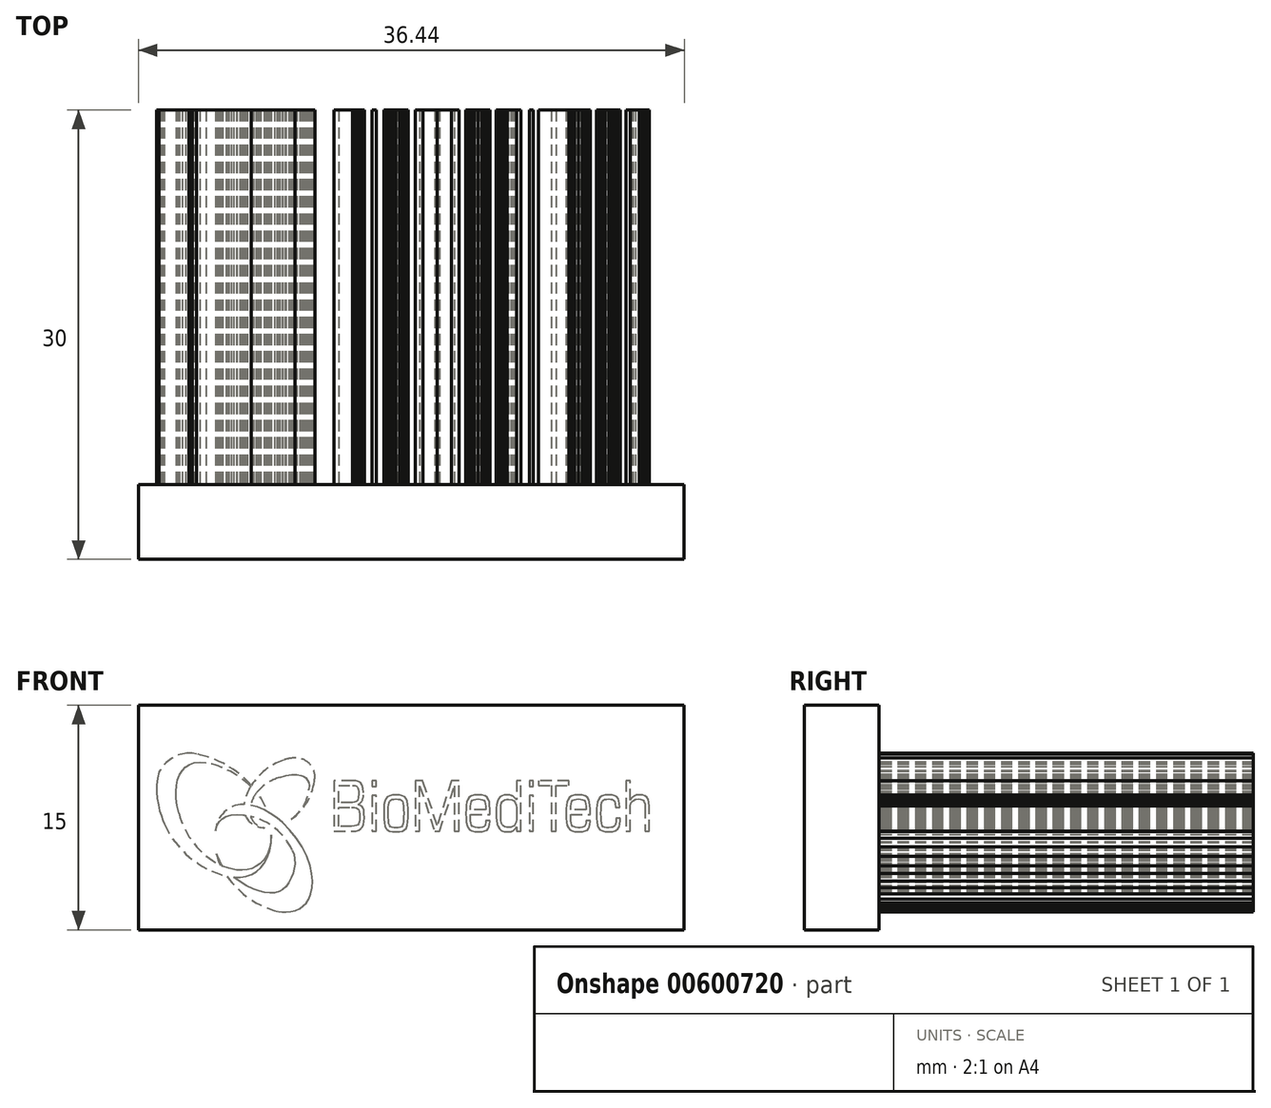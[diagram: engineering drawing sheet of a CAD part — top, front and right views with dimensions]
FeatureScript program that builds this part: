
annotation { "Feature Type Name" : "Feature", "Feature Type Description" : "" }
export const myFeature = defineFeature(function(context is Context, id is Id, definition is map)
    precondition{}
    {
        {
            var Q0;
            Q0=qCreatedBy(makeId("Front.planeOp"),FACE);
            var sketch = newSketch(context, id + "F0", { "sketchPlane" : qUnion([Q0])});
            skLineSegment(sketch, "E0", {"start": v(36.62, 94.25) * mm, "end": v(36.5, 94.75) * mm});
            skLineSegment(sketch, "E1", {"start": v(36.5, 94.75) * mm, "end": v(36.44, 95.22) * mm});
            skLineSegment(sketch, "E2", {"start": v(36.44, 95.22) * mm, "end": v(36.42, 95.67) * mm});
            skLineSegment(sketch, "E3", {"start": v(36.42, 95.67) * mm, "end": v(36.45, 96.09) * mm});
            skLineSegment(sketch, "E4", {"start": v(36.45, 96.09) * mm, "end": v(36.53, 96.47) * mm});
            skLineSegment(sketch, "E5", {"start": v(36.53, 96.47) * mm, "end": v(36.65, 96.8) * mm});
            skLineSegment(sketch, "E6", {"start": v(36.65, 96.8) * mm, "end": v(36.83, 97.1) * mm});
            skLineSegment(sketch, "E7", {"start": v(36.83, 97.1) * mm, "end": v(37.05, 97.32) * mm});
            skLineSegment(sketch, "E8", {"start": v(37.05, 97.32) * mm, "end": v(37.33, 97.5) * mm});
            skLineSegment(sketch, "E9", {"start": v(37.33, 97.5) * mm, "end": v(37.65, 97.6) * mm});
            skLineSegment(sketch, "E10", {"start": v(37.65, 97.6) * mm, "end": v(38.01, 97.64) * mm});
            skLineSegment(sketch, "E11", {"start": v(38.01, 97.64) * mm, "end": v(38.43, 97.6) * mm});
            skLineSegment(sketch, "E12", {"start": v(39.27, 91.03) * mm, "end": v(39.33, 90.89) * mm});
            skLineSegment(sketch, "E13", {"start": v(39.33, 90.89) * mm, "end": v(39.38, 90.77) * mm});
            skLineSegment(sketch, "E14", {"start": v(39.55, 90.7) * mm, "end": v(39.43, 90.89) * mm});
            skLineSegment(sketch, "E15", {"start": v(39.43, 90.89) * mm, "end": v(39.35, 91.03) * mm});
            skLineSegment(sketch, "E16", {"start": v(40.46, 90.45) * mm, "end": v(39.95, 90.56) * mm});
            skLineSegment(sketch, "E17", {"start": v(39.95, 90.56) * mm, "end": v(39.55, 90.7) * mm});
            skLineSegment(sketch, "E18", {"start": v(42.79, 92.79) * mm, "end": v(42.76, 92.31) * mm});
            skLineSegment(sketch, "E19", {"start": v(42.76, 92.31) * mm, "end": v(42.67, 91.88) * mm});
            skLineSegment(sketch, "E20", {"start": v(42.67, 91.88) * mm, "end": v(42.51, 91.48) * mm});
            skLineSegment(sketch, "E21", {"start": v(42.51, 91.48) * mm, "end": v(42.3, 91.14) * mm});
            skLineSegment(sketch, "E22", {"start": v(42.3, 91.14) * mm, "end": v(42.03, 90.86) * mm});
            skLineSegment(sketch, "E23", {"start": v(42.03, 90.86) * mm, "end": v(41.78, 90.68) * mm});
            skLineSegment(sketch, "E24", {"start": v(41.78, 90.68) * mm, "end": v(41.5, 90.55) * mm});
            skLineSegment(sketch, "E25", {"start": v(41.5, 90.55) * mm, "end": v(41.18, 90.46) * mm});
            skLineSegment(sketch, "E26", {"start": v(41.18, 90.46) * mm, "end": v(40.84, 90.43) * mm});
            skLineSegment(sketch, "E27", {"start": v(40.84, 90.43) * mm, "end": v(40.46, 90.45) * mm});
            skLineSegment(sketch, "E28", {"start": v(40.27, 89.97) * mm, "end": v(40.7, 89.97) * mm});
            skLineSegment(sketch, "E29", {"start": v(40.7, 89.97) * mm, "end": v(41.1, 90.04) * mm});
            skLineSegment(sketch, "E30", {"start": v(41.1, 90.04) * mm, "end": v(41.47, 90.17) * mm});
            skLineSegment(sketch, "E31", {"start": v(41.47, 90.17) * mm, "end": v(41.8, 90.36) * mm});
            skLineSegment(sketch, "E32", {"start": v(41.8, 90.36) * mm, "end": v(42.07, 90.6) * mm});
            skLineSegment(sketch, "E33", {"start": v(42.07, 90.6) * mm, "end": v(42.3, 90.9) * mm});
            skLineSegment(sketch, "E34", {"start": v(42.3, 90.9) * mm, "end": v(42.53, 91.3) * mm});
            skLineSegment(sketch, "E35", {"start": v(42.53, 91.3) * mm, "end": v(42.68, 91.75) * mm});
            skLineSegment(sketch, "E36", {"start": v(42.68, 91.75) * mm, "end": v(42.77, 92.25) * mm});
            skLineSegment(sketch, "E37", {"start": v(42.77, 92.25) * mm, "end": v(42.79, 92.79) * mm});
            skLineSegment(sketch, "E38", {"start": v(43.31, 89) * mm, "end": v(43.01, 88.93) * mm});
            skLineSegment(sketch, "E39", {"start": v(43.01, 88.93) * mm, "end": v(42.68, 88.92) * mm});
            skLineSegment(sketch, "E40", {"start": v(42.68, 88.92) * mm, "end": v(42.34, 88.96) * mm});
            skLineSegment(sketch, "E41", {"start": v(42.34, 88.96) * mm, "end": v(41.98, 89.05) * mm});
            skLineSegment(sketch, "E42", {"start": v(41.98, 89.05) * mm, "end": v(41.61, 89.17) * mm});
            skLineSegment(sketch, "E43", {"start": v(41.61, 89.17) * mm, "end": v(41.14, 89.4) * mm});
            skLineSegment(sketch, "E44", {"start": v(41.14, 89.4) * mm, "end": v(40.69, 89.67) * mm});
            skLineSegment(sketch, "E45", {"start": v(40.69, 89.67) * mm, "end": v(40.27, 89.97) * mm});
            skLineSegment(sketch, "E46", {"start": v(44.18, 91.79) * mm, "end": v(44.3, 91.5) * mm});
            skLineSegment(sketch, "E47", {"start": v(44.3, 91.5) * mm, "end": v(44.35, 91.19) * mm});
            skLineSegment(sketch, "E48", {"start": v(44.35, 91.19) * mm, "end": v(44.36, 90.87) * mm});
            skLineSegment(sketch, "E49", {"start": v(44.36, 90.87) * mm, "end": v(44.32, 90.55) * mm});
            skLineSegment(sketch, "E50", {"start": v(44.32, 90.55) * mm, "end": v(44.24, 90.23) * mm});
            skLineSegment(sketch, "E51", {"start": v(44.24, 90.23) * mm, "end": v(44.13, 89.93) * mm});
            skLineSegment(sketch, "E52", {"start": v(44.13, 89.93) * mm, "end": v(43.96, 89.61) * mm});
            skLineSegment(sketch, "E53", {"start": v(43.96, 89.61) * mm, "end": v(43.77, 89.34) * mm});
            skLineSegment(sketch, "E54", {"start": v(43.77, 89.34) * mm, "end": v(43.55, 89.13) * mm});
            skLineSegment(sketch, "E55", {"start": v(43.55, 89.13) * mm, "end": v(43.31, 89) * mm});
            skLineSegment(sketch, "E56", {"start": v(40.9, 94.12) * mm, "end": v(40.98, 94.11) * mm});
            skLineSegment(sketch, "E57", {"start": v(40.98, 94.11) * mm, "end": v(41.04, 94.1) * mm});
            skLineSegment(sketch, "E58", {"start": v(39.07, 93.1) * mm, "end": v(39.16, 93.42) * mm});
            skLineSegment(sketch, "E59", {"start": v(39.16, 93.42) * mm, "end": v(39.32, 93.68) * mm});
            skLineSegment(sketch, "E60", {"start": v(39.32, 93.68) * mm, "end": v(39.52, 93.88) * mm});
            skLineSegment(sketch, "E61", {"start": v(39.52, 93.88) * mm, "end": v(39.78, 94.03) * mm});
            skLineSegment(sketch, "E62", {"start": v(39.78, 94.03) * mm, "end": v(40.1, 94.12) * mm});
            skLineSegment(sketch, "E63", {"start": v(40.1, 94.12) * mm, "end": v(40.48, 94.15) * mm});
            skLineSegment(sketch, "E64", {"start": v(40.48, 94.15) * mm, "end": v(40.9, 94.12) * mm});
            skLineSegment(sketch, "E65", {"start": v(40.97, 94.83) * mm, "end": v(40.93, 94.83) * mm});
            skLineSegment(sketch, "E66", {"start": v(40.93, 94.83) * mm, "end": v(40.9, 94.83) * mm});
            skLineSegment(sketch, "E67", {"start": v(45.37, 90.73) * mm, "end": v(45.15, 91.38) * mm});
            skLineSegment(sketch, "E68", {"start": v(45.15, 91.38) * mm, "end": v(44.84, 92) * mm});
            skLineSegment(sketch, "E69", {"start": v(44.84, 92) * mm, "end": v(44.47, 92.58) * mm});
            skLineSegment(sketch, "E70", {"start": v(44.47, 92.58) * mm, "end": v(44.04, 93.12) * mm});
            skLineSegment(sketch, "E71", {"start": v(44.04, 93.12) * mm, "end": v(43.56, 93.6) * mm});
            skLineSegment(sketch, "E72", {"start": v(43.56, 93.6) * mm, "end": v(43.15, 93.94) * mm});
            skLineSegment(sketch, "E73", {"start": v(43.15, 93.94) * mm, "end": v(42.73, 94.23) * mm});
            skLineSegment(sketch, "E74", {"start": v(42.73, 94.23) * mm, "end": v(42.3, 94.47) * mm});
            skLineSegment(sketch, "E75", {"start": v(42.3, 94.47) * mm, "end": v(41.86, 94.65) * mm});
            skLineSegment(sketch, "E76", {"start": v(41.86, 94.65) * mm, "end": v(41.41, 94.77) * mm});
            skLineSegment(sketch, "E77", {"start": v(43.76, 87.64) * mm, "end": v(44.1, 87.67) * mm});
            skLineSegment(sketch, "E78", {"start": v(44.1, 87.67) * mm, "end": v(44.4, 87.75) * mm});
            skLineSegment(sketch, "E79", {"start": v(44.4, 87.75) * mm, "end": v(44.68, 87.88) * mm});
            skLineSegment(sketch, "E80", {"start": v(44.68, 87.88) * mm, "end": v(44.92, 88.05) * mm});
            skLineSegment(sketch, "E81", {"start": v(44.92, 88.05) * mm, "end": v(45.12, 88.26) * mm});
            skLineSegment(sketch, "E82", {"start": v(45.12, 88.26) * mm, "end": v(45.29, 88.51) * mm});
            skLineSegment(sketch, "E83", {"start": v(45.29, 88.51) * mm, "end": v(45.43, 88.87) * mm});
            skLineSegment(sketch, "E84", {"start": v(45.43, 88.87) * mm, "end": v(45.52, 89.27) * mm});
            skLineSegment(sketch, "E85", {"start": v(45.52, 89.27) * mm, "end": v(45.54, 89.72) * mm});
            skLineSegment(sketch, "E86", {"start": v(45.54, 89.72) * mm, "end": v(45.49, 90.2) * mm});
            skLineSegment(sketch, "E87", {"start": v(45.49, 90.2) * mm, "end": v(45.37, 90.73) * mm});
            skLineSegment(sketch, "E88", {"start": v(43.25, 87.68) * mm, "end": v(43.5, 87.65) * mm});
            skLineSegment(sketch, "E89", {"start": v(43.5, 87.65) * mm, "end": v(43.7, 87.64) * mm});
            skLineSegment(sketch, "E90", {"start": v(35.3, 97.01) * mm, "end": v(35.19, 96.57) * mm});
            skLineSegment(sketch, "E91", {"start": v(35.19, 96.57) * mm, "end": v(35.13, 96.12) * mm});
            skLineSegment(sketch, "E92", {"start": v(35.13, 96.12) * mm, "end": v(35.13, 95.67) * mm});
            skLineSegment(sketch, "E93", {"start": v(35.13, 95.67) * mm, "end": v(35.17, 95.22) * mm});
            skLineSegment(sketch, "E94", {"start": v(35.17, 95.22) * mm, "end": v(35.24, 94.8) * mm});
            skLineSegment(sketch, "E95", {"start": v(35.24, 94.8) * mm, "end": v(35.33, 94.42) * mm});
            skLineSegment(sketch, "E96", {"start": v(35.33, 94.42) * mm, "end": v(35.44, 94.08) * mm});
            skLineSegment(sketch, "E97", {"start": v(35.44, 94.08) * mm, "end": v(35.54, 93.79) * mm});
            skLineSegment(sketch, "E98", {"start": v(35.54, 93.79) * mm, "end": v(35.63, 93.55) * mm});
            skLineSegment(sketch, "E99", {"start": v(37.8, 98.2) * mm, "end": v(37.51, 98.24) * mm});
            skLineSegment(sketch, "E100", {"start": v(37.51, 98.24) * mm, "end": v(37.3, 98.25) * mm});
            skLineSegment(sketch, "E101", {"start": v(43.35, 96.64) * mm, "end": v(43.76, 96.76) * mm});
            skLineSegment(sketch, "E102", {"start": v(43.76, 96.76) * mm, "end": v(44.14, 96.82) * mm});
            skLineSegment(sketch, "E103", {"start": v(44.14, 96.82) * mm, "end": v(44.5, 96.83) * mm});
            skLineSegment(sketch, "E104", {"start": v(44.5, 96.83) * mm, "end": v(44.8, 96.77) * mm});
            skLineSegment(sketch, "E105", {"start": v(44.8, 96.77) * mm, "end": v(44.96, 96.7) * mm});
            skLineSegment(sketch, "E106", {"start": v(44.96, 96.7) * mm, "end": v(45.1, 96.6) * mm});
            skLineSegment(sketch, "E107", {"start": v(45.1, 96.6) * mm, "end": v(45.21, 96.46) * mm});
            skLineSegment(sketch, "E108", {"start": v(45.21, 96.46) * mm, "end": v(45.28, 96.29) * mm});
            skLineSegment(sketch, "E109", {"start": v(45.28, 96.29) * mm, "end": v(45.31, 96.08) * mm});
            skLineSegment(sketch, "E110", {"start": v(45.31, 96.08) * mm, "end": v(45.3, 95.84) * mm});
            skLineSegment(sketch, "E111", {"start": v(67.32, 95.2) * mm, "end": v(67.44, 95.18) * mm});
            skLineSegment(sketch, "E112", {"start": v(67.44, 95.18) * mm, "end": v(67.54, 95.15) * mm});
            skLineSegment(sketch, "E113", {"start": v(67.54, 95.15) * mm, "end": v(67.62, 95.1) * mm});
            skLineSegment(sketch, "E114", {"start": v(67.62, 95.1) * mm, "end": v(67.67, 95.03) * mm});
            skLineSegment(sketch, "E115", {"start": v(67.67, 95.03) * mm, "end": v(67.73, 94.86) * mm});
            skLineSegment(sketch, "E116", {"start": v(67.73, 94.86) * mm, "end": v(67.74, 94.65) * mm});
            skLineSegment(sketch, "E117", {"start": v(66.75, 94.55) * mm, "end": v(66.76, 94.74) * mm});
            skLineSegment(sketch, "E118", {"start": v(66.76, 94.74) * mm, "end": v(66.8, 94.9) * mm});
            skLineSegment(sketch, "E119", {"start": v(66.8, 94.9) * mm, "end": v(66.86, 95) * mm});
            skLineSegment(sketch, "E120", {"start": v(66.86, 95) * mm, "end": v(66.94, 95.1) * mm});
            skLineSegment(sketch, "E121", {"start": v(66.94, 95.1) * mm, "end": v(67.11, 95.17) * mm});
            skLineSegment(sketch, "E122", {"start": v(67.11, 95.17) * mm, "end": v(67.32, 95.2) * mm});
            skLineSegment(sketch, "E123", {"start": v(68.02, 94.73) * mm, "end": v(68, 94.96) * mm});
            skLineSegment(sketch, "E124", {"start": v(68, 94.96) * mm, "end": v(67.95, 95.16) * mm});
            skLineSegment(sketch, "E125", {"start": v(67.95, 95.16) * mm, "end": v(67.85, 95.31) * mm});
            skLineSegment(sketch, "E126", {"start": v(67.85, 95.31) * mm, "end": v(67.73, 95.4) * mm});
            skLineSegment(sketch, "E127", {"start": v(67.73, 95.4) * mm, "end": v(67.57, 95.45) * mm});
            skLineSegment(sketch, "E128", {"start": v(67.57, 95.45) * mm, "end": v(67.37, 95.46) * mm});
            skLineSegment(sketch, "E129", {"start": v(65.31, 93.28) * mm, "end": v(65.16, 93.28) * mm});
            skLineSegment(sketch, "E130", {"start": v(65.16, 93.28) * mm, "end": v(65.04, 93.3) * mm});
            skLineSegment(sketch, "E131", {"start": v(65.04, 93.3) * mm, "end": v(64.95, 93.35) * mm});
            skLineSegment(sketch, "E132", {"start": v(64.95, 93.35) * mm, "end": v(64.89, 93.42) * mm});
            skLineSegment(sketch, "E133", {"start": v(64.89, 93.42) * mm, "end": v(64.84, 93.56) * mm});
            skLineSegment(sketch, "E134", {"start": v(64.84, 93.56) * mm, "end": v(64.81, 93.76) * mm});
            skLineSegment(sketch, "E135", {"start": v(64.81, 93.76) * mm, "end": v(64.8, 93.97) * mm});
            skLineSegment(sketch, "E136", {"start": v(64.8, 93.97) * mm, "end": v(64.8, 94.24) * mm});
            skLineSegment(sketch, "E137", {"start": v(65.8, 93.9) * mm, "end": v(65.8, 93.7) * mm});
            skLineSegment(sketch, "E138", {"start": v(65.8, 93.7) * mm, "end": v(65.77, 93.53) * mm});
            skLineSegment(sketch, "E139", {"start": v(65.77, 93.53) * mm, "end": v(65.73, 93.44) * mm});
            skLineSegment(sketch, "E140", {"start": v(65.73, 93.44) * mm, "end": v(65.68, 93.37) * mm});
            skLineSegment(sketch, "E141", {"start": v(65.68, 93.37) * mm, "end": v(65.6, 93.32) * mm});
            skLineSegment(sketch, "E142", {"start": v(65.6, 93.32) * mm, "end": v(65.47, 93.29) * mm});
            skLineSegment(sketch, "E143", {"start": v(65.47, 93.29) * mm, "end": v(65.31, 93.28) * mm});
            skLineSegment(sketch, "E144", {"start": v(65.31, 93) * mm, "end": v(65.57, 93.02) * mm});
            skLineSegment(sketch, "E145", {"start": v(65.57, 93.02) * mm, "end": v(65.77, 93.08) * mm});
            skLineSegment(sketch, "E146", {"start": v(65.77, 93.08) * mm, "end": v(65.93, 93.2) * mm});
            skLineSegment(sketch, "E147", {"start": v(65.93, 93.2) * mm, "end": v(66.01, 93.33) * mm});
            skLineSegment(sketch, "E148", {"start": v(66.01, 93.33) * mm, "end": v(66.06, 93.51) * mm});
            skLineSegment(sketch, "E149", {"start": v(66.06, 93.51) * mm, "end": v(66.08, 93.75) * mm});
            skLineSegment(sketch, "E150", {"start": v(64.5, 94.24) * mm, "end": v(64.5, 93.9) * mm});
            skLineSegment(sketch, "E151", {"start": v(64.5, 93.9) * mm, "end": v(64.52, 93.64) * mm});
            skLineSegment(sketch, "E152", {"start": v(64.52, 93.64) * mm, "end": v(64.56, 93.42) * mm});
            skLineSegment(sketch, "E153", {"start": v(64.56, 93.42) * mm, "end": v(64.63, 93.26) * mm});
            skLineSegment(sketch, "E154", {"start": v(64.63, 93.26) * mm, "end": v(64.73, 93.14) * mm});
            skLineSegment(sketch, "E155", {"start": v(64.73, 93.14) * mm, "end": v(64.88, 93.06) * mm});
            skLineSegment(sketch, "E156", {"start": v(64.88, 93.06) * mm, "end": v(65.07, 93.02) * mm});
            skLineSegment(sketch, "E157", {"start": v(65.07, 93.02) * mm, "end": v(65.31, 93) * mm});
            skLineSegment(sketch, "E158", {"start": v(65.31, 95.46) * mm, "end": v(65.06, 95.45) * mm});
            skLineSegment(sketch, "E159", {"start": v(65.06, 95.45) * mm, "end": v(64.86, 95.4) * mm});
            skLineSegment(sketch, "E160", {"start": v(64.86, 95.4) * mm, "end": v(64.72, 95.3) * mm});
            skLineSegment(sketch, "E161", {"start": v(64.72, 95.3) * mm, "end": v(64.61, 95.15) * mm});
            skLineSegment(sketch, "E162", {"start": v(64.61, 95.15) * mm, "end": v(64.56, 94.99) * mm});
            skLineSegment(sketch, "E163", {"start": v(64.56, 94.99) * mm, "end": v(64.52, 94.78) * mm});
            skLineSegment(sketch, "E164", {"start": v(64.52, 94.78) * mm, "end": v(64.5, 94.53) * mm});
            skLineSegment(sketch, "E165", {"start": v(64.5, 94.53) * mm, "end": v(64.5, 94.24) * mm});
            skLineSegment(sketch, "E166", {"start": v(66.04, 94.63) * mm, "end": v(66.03, 94.87) * mm});
            skLineSegment(sketch, "E167", {"start": v(66.03, 94.87) * mm, "end": v(66, 95.07) * mm});
            skLineSegment(sketch, "E168", {"start": v(66, 95.07) * mm, "end": v(65.95, 95.22) * mm});
            skLineSegment(sketch, "E169", {"start": v(65.95, 95.22) * mm, "end": v(65.86, 95.33) * mm});
            skLineSegment(sketch, "E170", {"start": v(65.86, 95.33) * mm, "end": v(65.73, 95.4) * mm});
            skLineSegment(sketch, "E171", {"start": v(65.73, 95.4) * mm, "end": v(65.55, 95.45) * mm});
            skLineSegment(sketch, "E172", {"start": v(65.55, 95.45) * mm, "end": v(65.31, 95.46) * mm});
            skLineSegment(sketch, "E173", {"start": v(65.31, 95.2) * mm, "end": v(65.45, 95.18) * mm});
            skLineSegment(sketch, "E174", {"start": v(65.45, 95.18) * mm, "end": v(65.56, 95.16) * mm});
            skLineSegment(sketch, "E175", {"start": v(65.56, 95.16) * mm, "end": v(65.64, 95.11) * mm});
            skLineSegment(sketch, "E176", {"start": v(65.64, 95.11) * mm, "end": v(65.7, 95.04) * mm});
            skLineSegment(sketch, "E177", {"start": v(65.7, 95.04) * mm, "end": v(65.75, 94.88) * mm});
            skLineSegment(sketch, "E178", {"start": v(65.75, 94.88) * mm, "end": v(65.76, 94.63) * mm});
            skLineSegment(sketch, "E179", {"start": v(64.8, 94.24) * mm, "end": v(64.8, 94.46) * mm});
            skLineSegment(sketch, "E180", {"start": v(64.8, 94.46) * mm, "end": v(64.8, 94.65) * mm});
            skLineSegment(sketch, "E181", {"start": v(64.8, 94.65) * mm, "end": v(64.82, 94.8) * mm});
            skLineSegment(sketch, "E182", {"start": v(64.82, 94.8) * mm, "end": v(64.85, 94.94) * mm});
            skLineSegment(sketch, "E183", {"start": v(64.85, 94.94) * mm, "end": v(64.89, 95.05) * mm});
            skLineSegment(sketch, "E184", {"start": v(64.89, 95.05) * mm, "end": v(64.95, 95.12) * mm});
            skLineSegment(sketch, "E185", {"start": v(64.95, 95.12) * mm, "end": v(65.04, 95.17) * mm});
            skLineSegment(sketch, "E186", {"start": v(65.04, 95.17) * mm, "end": v(65.16, 95.19) * mm});
            skLineSegment(sketch, "E187", {"start": v(65.16, 95.19) * mm, "end": v(65.31, 95.2) * mm});
            skLineSegment(sketch, "E188", {"start": v(63.29, 95.2) * mm, "end": v(63.45, 95.18) * mm});
            skLineSegment(sketch, "E189", {"start": v(63.45, 95.18) * mm, "end": v(63.57, 95.15) * mm});
            skLineSegment(sketch, "E190", {"start": v(63.57, 95.15) * mm, "end": v(63.66, 95.1) * mm});
            skLineSegment(sketch, "E191", {"start": v(63.66, 95.1) * mm, "end": v(63.73, 95.02) * mm});
            skLineSegment(sketch, "E192", {"start": v(63.73, 95.02) * mm, "end": v(63.77, 94.88) * mm});
            skLineSegment(sketch, "E193", {"start": v(63.77, 94.88) * mm, "end": v(63.79, 94.7) * mm});
            skLineSegment(sketch, "E194", {"start": v(63.79, 94.7) * mm, "end": v(63.8, 94.46) * mm});
            skLineSegment(sketch, "E195", {"start": v(62.78, 94.46) * mm, "end": v(62.78, 94.7) * mm});
            skLineSegment(sketch, "E196", {"start": v(62.78, 94.7) * mm, "end": v(62.8, 94.88) * mm});
            skLineSegment(sketch, "E197", {"start": v(62.8, 94.88) * mm, "end": v(62.85, 95.02) * mm});
            skLineSegment(sketch, "E198", {"start": v(62.85, 95.02) * mm, "end": v(62.9, 95.1) * mm});
            skLineSegment(sketch, "E199", {"start": v(62.9, 95.1) * mm, "end": v(63, 95.15) * mm});
            skLineSegment(sketch, "E200", {"start": v(63, 95.15) * mm, "end": v(63.12, 95.18) * mm});
            skLineSegment(sketch, "E201", {"start": v(63.12, 95.18) * mm, "end": v(63.29, 95.2) * mm});
            skLineSegment(sketch, "E202", {"start": v(63.3, 93) * mm, "end": v(63.57, 93.02) * mm});
            skLineSegment(sketch, "E203", {"start": v(63.57, 93.02) * mm, "end": v(63.77, 93.06) * mm});
            skLineSegment(sketch, "E204", {"start": v(63.77, 93.06) * mm, "end": v(63.89, 93.12) * mm});
            skLineSegment(sketch, "E205", {"start": v(63.89, 93.12) * mm, "end": v(63.97, 93.2) * mm});
            skLineSegment(sketch, "E206", {"start": v(63.97, 93.2) * mm, "end": v(64.03, 93.32) * mm});
            skLineSegment(sketch, "E207", {"start": v(64.03, 93.32) * mm, "end": v(64.06, 93.47) * mm});
            skLineSegment(sketch, "E208", {"start": v(64.06, 93.47) * mm, "end": v(64.07, 93.67) * mm});
            skLineSegment(sketch, "E209", {"start": v(62.48, 94.24) * mm, "end": v(62.48, 93.9) * mm});
            skLineSegment(sketch, "E210", {"start": v(62.48, 93.9) * mm, "end": v(62.5, 93.64) * mm});
            skLineSegment(sketch, "E211", {"start": v(62.5, 93.64) * mm, "end": v(62.54, 93.42) * mm});
            skLineSegment(sketch, "E212", {"start": v(62.54, 93.42) * mm, "end": v(62.61, 93.26) * mm});
            skLineSegment(sketch, "E213", {"start": v(62.61, 93.26) * mm, "end": v(62.71, 93.14) * mm});
            skLineSegment(sketch, "E214", {"start": v(62.71, 93.14) * mm, "end": v(62.86, 93.06) * mm});
            skLineSegment(sketch, "E215", {"start": v(62.86, 93.06) * mm, "end": v(63.05, 93.02) * mm});
            skLineSegment(sketch, "E216", {"start": v(63.05, 93.02) * mm, "end": v(63.3, 93) * mm});
            skLineSegment(sketch, "E217", {"start": v(63.3, 95.46) * mm, "end": v(63.04, 95.45) * mm});
            skLineSegment(sketch, "E218", {"start": v(63.04, 95.45) * mm, "end": v(62.85, 95.4) * mm});
            skLineSegment(sketch, "E219", {"start": v(62.85, 95.4) * mm, "end": v(62.7, 95.3) * mm});
            skLineSegment(sketch, "E220", {"start": v(62.7, 95.3) * mm, "end": v(62.6, 95.15) * mm});
            skLineSegment(sketch, "E221", {"start": v(62.6, 95.15) * mm, "end": v(62.54, 94.99) * mm});
            skLineSegment(sketch, "E222", {"start": v(62.54, 94.99) * mm, "end": v(62.5, 94.78) * mm});
            skLineSegment(sketch, "E223", {"start": v(62.5, 94.78) * mm, "end": v(62.48, 94.53) * mm});
            skLineSegment(sketch, "E224", {"start": v(62.48, 94.53) * mm, "end": v(62.48, 94.24) * mm});
            skLineSegment(sketch, "E225", {"start": v(64.07, 94.52) * mm, "end": v(64.06, 94.78) * mm});
            skLineSegment(sketch, "E226", {"start": v(64.06, 94.78) * mm, "end": v(64.04, 94.99) * mm});
            skLineSegment(sketch, "E227", {"start": v(64.04, 94.99) * mm, "end": v(63.98, 95.16) * mm});
            skLineSegment(sketch, "E228", {"start": v(63.98, 95.16) * mm, "end": v(63.89, 95.29) * mm});
            skLineSegment(sketch, "E229", {"start": v(63.89, 95.29) * mm, "end": v(63.75, 95.39) * mm});
            skLineSegment(sketch, "E230", {"start": v(63.75, 95.39) * mm, "end": v(63.55, 95.44) * mm});
            skLineSegment(sketch, "E231", {"start": v(63.55, 95.44) * mm, "end": v(63.3, 95.46) * mm});
            skLineSegment(sketch, "E232", {"start": v(63.25, 93.28) * mm, "end": v(63.1, 93.29) * mm});
            skLineSegment(sketch, "E233", {"start": v(63.1, 93.29) * mm, "end": v(63, 93.32) * mm});
            skLineSegment(sketch, "E234", {"start": v(63, 93.32) * mm, "end": v(62.9, 93.37) * mm});
            skLineSegment(sketch, "E235", {"start": v(62.9, 93.37) * mm, "end": v(62.85, 93.46) * mm});
            skLineSegment(sketch, "E236", {"start": v(62.85, 93.46) * mm, "end": v(62.8, 93.58) * mm});
            skLineSegment(sketch, "E237", {"start": v(62.8, 93.58) * mm, "end": v(62.79, 93.74) * mm});
            skLineSegment(sketch, "E238", {"start": v(62.79, 93.74) * mm, "end": v(62.78, 93.95) * mm});
            skLineSegment(sketch, "E239", {"start": v(63.8, 93.75) * mm, "end": v(63.79, 93.61) * mm});
            skLineSegment(sketch, "E240", {"start": v(63.79, 93.61) * mm, "end": v(63.77, 93.5) * mm});
            skLineSegment(sketch, "E241", {"start": v(63.77, 93.5) * mm, "end": v(63.75, 93.42) * mm});
            skLineSegment(sketch, "E242", {"start": v(63.75, 93.42) * mm, "end": v(63.71, 93.36) * mm});
            skLineSegment(sketch, "E243", {"start": v(63.71, 93.36) * mm, "end": v(63.66, 93.32) * mm});
            skLineSegment(sketch, "E244", {"start": v(63.66, 93.32) * mm, "end": v(63.56, 93.3) * mm});
            skLineSegment(sketch, "E245", {"start": v(63.56, 93.3) * mm, "end": v(63.42, 93.28) * mm});
            skLineSegment(sketch, "E246", {"start": v(63.42, 93.28) * mm, "end": v(63.25, 93.28) * mm});
            skLineSegment(sketch, "E247", {"start": v(58.54, 95.46) * mm, "end": v(58.35, 95.45) * mm});
            skLineSegment(sketch, "E248", {"start": v(58.35, 95.45) * mm, "end": v(58.19, 95.4) * mm});
            skLineSegment(sketch, "E249", {"start": v(58.19, 95.4) * mm, "end": v(58.06, 95.32) * mm});
            skLineSegment(sketch, "E250", {"start": v(58.06, 95.32) * mm, "end": v(57.96, 95.2) * mm});
            skLineSegment(sketch, "E251", {"start": v(57.96, 95.2) * mm, "end": v(57.88, 95.03) * mm});
            skLineSegment(sketch, "E252", {"start": v(57.88, 95.03) * mm, "end": v(57.84, 94.82) * mm});
            skLineSegment(sketch, "E253", {"start": v(57.84, 94.82) * mm, "end": v(57.8, 94.56) * mm});
            skLineSegment(sketch, "E254", {"start": v(57.8, 94.56) * mm, "end": v(57.8, 94.24) * mm});
            skLineSegment(sketch, "E255", {"start": v(58.64, 95.16) * mm, "end": v(58.83, 95.14) * mm});
            skLineSegment(sketch, "E256", {"start": v(58.83, 95.14) * mm, "end": v(58.98, 95.07) * mm});
            skLineSegment(sketch, "E257", {"start": v(58.98, 95.07) * mm, "end": v(59.08, 94.94) * mm});
            skLineSegment(sketch, "E258", {"start": v(59.08, 94.94) * mm, "end": v(59.13, 94.8) * mm});
            skLineSegment(sketch, "E259", {"start": v(59.13, 94.8) * mm, "end": v(59.16, 94.6) * mm});
            skLineSegment(sketch, "E260", {"start": v(59.16, 94.6) * mm, "end": v(59.17, 94.38) * mm});
            skLineSegment(sketch, "E261", {"start": v(58.1, 94.24) * mm, "end": v(58.11, 94.54) * mm});
            skLineSegment(sketch, "E262", {"start": v(58.11, 94.54) * mm, "end": v(58.13, 94.77) * mm});
            skLineSegment(sketch, "E263", {"start": v(58.13, 94.77) * mm, "end": v(58.16, 94.9) * mm});
            skLineSegment(sketch, "E264", {"start": v(58.16, 94.9) * mm, "end": v(58.2, 95) * mm});
            skLineSegment(sketch, "E265", {"start": v(58.2, 95) * mm, "end": v(58.28, 95.09) * mm});
            skLineSegment(sketch, "E266", {"start": v(58.28, 95.09) * mm, "end": v(58.37, 95.13) * mm});
            skLineSegment(sketch, "E267", {"start": v(58.37, 95.13) * mm, "end": v(58.49, 95.16) * mm});
            skLineSegment(sketch, "E268", {"start": v(58.49, 95.16) * mm, "end": v(58.64, 95.16) * mm});
            skLineSegment(sketch, "E269", {"start": v(58.64, 93.3) * mm, "end": v(58.49, 93.31) * mm});
            skLineSegment(sketch, "E270", {"start": v(58.49, 93.31) * mm, "end": v(58.37, 93.34) * mm});
            skLineSegment(sketch, "E271", {"start": v(58.37, 93.34) * mm, "end": v(58.28, 93.38) * mm});
            skLineSegment(sketch, "E272", {"start": v(58.28, 93.38) * mm, "end": v(58.2, 93.46) * mm});
            skLineSegment(sketch, "E273", {"start": v(58.2, 93.46) * mm, "end": v(58.15, 93.6) * mm});
            skLineSegment(sketch, "E274", {"start": v(58.15, 93.6) * mm, "end": v(58.12, 93.8) * mm});
            skLineSegment(sketch, "E275", {"start": v(58.12, 93.8) * mm, "end": v(58.1, 93.99) * mm});
            skLineSegment(sketch, "E276", {"start": v(58.1, 93.99) * mm, "end": v(58.1, 94.24) * mm});
            skLineSegment(sketch, "E277", {"start": v(59.17, 94.38) * mm, "end": v(59.16, 94.07) * mm});
            skLineSegment(sketch, "E278", {"start": v(59.16, 94.07) * mm, "end": v(59.15, 93.83) * mm});
            skLineSegment(sketch, "E279", {"start": v(59.15, 93.83) * mm, "end": v(59.12, 93.65) * mm});
            skLineSegment(sketch, "E280", {"start": v(59.12, 93.65) * mm, "end": v(59.08, 93.5) * mm});
            skLineSegment(sketch, "E281", {"start": v(59.08, 93.5) * mm, "end": v(59, 93.4) * mm});
            skLineSegment(sketch, "E282", {"start": v(59, 93.4) * mm, "end": v(58.92, 93.35) * mm});
            skLineSegment(sketch, "E283", {"start": v(58.92, 93.35) * mm, "end": v(58.8, 93.32) * mm});
            skLineSegment(sketch, "E284", {"start": v(58.8, 93.32) * mm, "end": v(58.64, 93.3) * mm});
            skLineSegment(sketch, "E285", {"start": v(57.8, 94.24) * mm, "end": v(57.8, 93.96) * mm});
            skLineSegment(sketch, "E286", {"start": v(57.8, 93.96) * mm, "end": v(57.82, 93.73) * mm});
            skLineSegment(sketch, "E287", {"start": v(57.82, 93.73) * mm, "end": v(57.86, 93.53) * mm});
            skLineSegment(sketch, "E288", {"start": v(57.86, 93.53) * mm, "end": v(57.92, 93.35) * mm});
            skLineSegment(sketch, "E289", {"start": v(57.92, 93.35) * mm, "end": v(58, 93.2) * mm});
            skLineSegment(sketch, "E290", {"start": v(58, 93.2) * mm, "end": v(58.15, 93.1) * mm});
            skLineSegment(sketch, "E291", {"start": v(58.15, 93.1) * mm, "end": v(58.34, 93.03) * mm});
            skLineSegment(sketch, "E292", {"start": v(58.34, 93.03) * mm, "end": v(58.59, 93) * mm});
            skLineSegment(sketch, "E293", {"start": v(56.6, 95.2) * mm, "end": v(56.76, 95.18) * mm});
            skLineSegment(sketch, "E294", {"start": v(56.76, 95.18) * mm, "end": v(56.88, 95.15) * mm});
            skLineSegment(sketch, "E295", {"start": v(56.88, 95.15) * mm, "end": v(56.97, 95.1) * mm});
            skLineSegment(sketch, "E296", {"start": v(56.97, 95.1) * mm, "end": v(57.03, 95.02) * mm});
            skLineSegment(sketch, "E297", {"start": v(57.03, 95.02) * mm, "end": v(57.08, 94.88) * mm});
            skLineSegment(sketch, "E298", {"start": v(57.08, 94.88) * mm, "end": v(57.1, 94.7) * mm});
            skLineSegment(sketch, "E299", {"start": v(57.1, 94.7) * mm, "end": v(57.1, 94.46) * mm});
            skLineSegment(sketch, "E300", {"start": v(56.09, 94.46) * mm, "end": v(56.09, 94.7) * mm});
            skLineSegment(sketch, "E301", {"start": v(56.09, 94.7) * mm, "end": v(56.1, 94.88) * mm});
            skLineSegment(sketch, "E302", {"start": v(56.1, 94.88) * mm, "end": v(56.15, 95.02) * mm});
            skLineSegment(sketch, "E303", {"start": v(56.15, 95.02) * mm, "end": v(56.21, 95.1) * mm});
            skLineSegment(sketch, "E304", {"start": v(56.21, 95.1) * mm, "end": v(56.3, 95.15) * mm});
            skLineSegment(sketch, "E305", {"start": v(56.3, 95.15) * mm, "end": v(56.43, 95.18) * mm});
            skLineSegment(sketch, "E306", {"start": v(56.43, 95.18) * mm, "end": v(56.6, 95.2) * mm});
            skLineSegment(sketch, "E307", {"start": v(56.6, 93) * mm, "end": v(56.88, 93.02) * mm});
            skLineSegment(sketch, "E308", {"start": v(56.88, 93.02) * mm, "end": v(57.08, 93.06) * mm});
            skLineSegment(sketch, "E309", {"start": v(57.08, 93.06) * mm, "end": v(57.2, 93.12) * mm});
            skLineSegment(sketch, "E310", {"start": v(57.2, 93.12) * mm, "end": v(57.28, 93.2) * mm});
            skLineSegment(sketch, "E311", {"start": v(57.28, 93.2) * mm, "end": v(57.34, 93.32) * mm});
            skLineSegment(sketch, "E312", {"start": v(57.34, 93.32) * mm, "end": v(57.37, 93.47) * mm});
            skLineSegment(sketch, "E313", {"start": v(57.37, 93.47) * mm, "end": v(57.38, 93.67) * mm});
            skLineSegment(sketch, "E314", {"start": v(56.6, 95.46) * mm, "end": v(56.35, 95.45) * mm});
            skLineSegment(sketch, "E315", {"start": v(56.35, 95.45) * mm, "end": v(56.15, 95.4) * mm});
            skLineSegment(sketch, "E316", {"start": v(56.15, 95.4) * mm, "end": v(56, 95.3) * mm});
            skLineSegment(sketch, "E317", {"start": v(56, 95.3) * mm, "end": v(55.9, 95.15) * mm});
            skLineSegment(sketch, "E318", {"start": v(55.9, 95.15) * mm, "end": v(55.84, 94.99) * mm});
            skLineSegment(sketch, "E319", {"start": v(55.84, 94.99) * mm, "end": v(55.8, 94.78) * mm});
            skLineSegment(sketch, "E320", {"start": v(55.8, 94.78) * mm, "end": v(55.79, 94.53) * mm});
            skLineSegment(sketch, "E321", {"start": v(55.79, 94.53) * mm, "end": v(55.78, 94.24) * mm});
            skLineSegment(sketch, "E322", {"start": v(57.38, 94.52) * mm, "end": v(57.37, 94.78) * mm});
            skLineSegment(sketch, "E323", {"start": v(57.37, 94.78) * mm, "end": v(57.34, 94.99) * mm});
            skLineSegment(sketch, "E324", {"start": v(57.34, 94.99) * mm, "end": v(57.29, 95.16) * mm});
            skLineSegment(sketch, "E325", {"start": v(57.29, 95.16) * mm, "end": v(57.2, 95.29) * mm});
            skLineSegment(sketch, "E326", {"start": v(57.2, 95.29) * mm, "end": v(57.06, 95.39) * mm});
            skLineSegment(sketch, "E327", {"start": v(57.06, 95.39) * mm, "end": v(56.86, 95.44) * mm});
            skLineSegment(sketch, "E328", {"start": v(56.86, 95.44) * mm, "end": v(56.6, 95.46) * mm});
            skLineSegment(sketch, "E329", {"start": v(56.55, 93.28) * mm, "end": v(56.4, 93.29) * mm});
            skLineSegment(sketch, "E330", {"start": v(56.4, 93.29) * mm, "end": v(56.3, 93.32) * mm});
            skLineSegment(sketch, "E331", {"start": v(56.3, 93.32) * mm, "end": v(56.21, 93.37) * mm});
            skLineSegment(sketch, "E332", {"start": v(56.21, 93.37) * mm, "end": v(56.15, 93.46) * mm});
            skLineSegment(sketch, "E333", {"start": v(56.15, 93.46) * mm, "end": v(56.11, 93.58) * mm});
            skLineSegment(sketch, "E334", {"start": v(56.11, 93.58) * mm, "end": v(56.1, 93.74) * mm});
            skLineSegment(sketch, "E335", {"start": v(56.1, 93.74) * mm, "end": v(56.09, 93.95) * mm});
            skLineSegment(sketch, "E336", {"start": v(57.1, 93.75) * mm, "end": v(57.1, 93.61) * mm});
            skLineSegment(sketch, "E337", {"start": v(57.1, 93.61) * mm, "end": v(57.08, 93.5) * mm});
            skLineSegment(sketch, "E338", {"start": v(57.08, 93.5) * mm, "end": v(57.06, 93.42) * mm});
            skLineSegment(sketch, "E339", {"start": v(57.06, 93.42) * mm, "end": v(57.02, 93.36) * mm});
            skLineSegment(sketch, "E340", {"start": v(57.02, 93.36) * mm, "end": v(56.96, 93.32) * mm});
            skLineSegment(sketch, "E341", {"start": v(56.96, 93.32) * mm, "end": v(56.86, 93.3) * mm});
            skLineSegment(sketch, "E342", {"start": v(56.86, 93.3) * mm, "end": v(56.73, 93.28) * mm});
            skLineSegment(sketch, "E343", {"start": v(56.73, 93.28) * mm, "end": v(56.55, 93.28) * mm});
            skLineSegment(sketch, "E344", {"start": v(55.78, 94.24) * mm, "end": v(55.79, 93.9) * mm});
            skLineSegment(sketch, "E345", {"start": v(55.79, 93.9) * mm, "end": v(55.8, 93.64) * mm});
            skLineSegment(sketch, "E346", {"start": v(55.8, 93.64) * mm, "end": v(55.85, 93.42) * mm});
            skLineSegment(sketch, "E347", {"start": v(55.85, 93.42) * mm, "end": v(55.92, 93.26) * mm});
            skLineSegment(sketch, "E348", {"start": v(55.92, 93.26) * mm, "end": v(56.02, 93.14) * mm});
            skLineSegment(sketch, "E349", {"start": v(56.02, 93.14) * mm, "end": v(56.16, 93.06) * mm});
            skLineSegment(sketch, "E350", {"start": v(56.16, 93.06) * mm, "end": v(56.36, 93.02) * mm});
            skLineSegment(sketch, "E351", {"start": v(56.36, 93.02) * mm, "end": v(56.6, 93) * mm});
            skLineSegment(sketch, "E352", {"start": v(51.11, 93) * mm, "end": v(51.35, 93.02) * mm});
            skLineSegment(sketch, "E353", {"start": v(51.35, 93.02) * mm, "end": v(51.54, 93.06) * mm});
            skLineSegment(sketch, "E354", {"start": v(51.54, 93.06) * mm, "end": v(51.69, 93.14) * mm});
            skLineSegment(sketch, "E355", {"start": v(51.69, 93.14) * mm, "end": v(51.8, 93.25) * mm});
            skLineSegment(sketch, "E356", {"start": v(51.8, 93.25) * mm, "end": v(51.87, 93.44) * mm});
            skLineSegment(sketch, "E357", {"start": v(51.87, 93.44) * mm, "end": v(51.91, 93.69) * mm});
            skLineSegment(sketch, "E358", {"start": v(51.91, 93.69) * mm, "end": v(51.93, 93.94) * mm});
            skLineSegment(sketch, "E359", {"start": v(51.93, 93.94) * mm, "end": v(51.93, 94.24) * mm});
            skLineSegment(sketch, "E360", {"start": v(51.11, 95.2) * mm, "end": v(51.26, 95.19) * mm});
            skLineSegment(sketch, "E361", {"start": v(51.26, 95.19) * mm, "end": v(51.38, 95.17) * mm});
            skLineSegment(sketch, "E362", {"start": v(51.38, 95.17) * mm, "end": v(51.47, 95.12) * mm});
            skLineSegment(sketch, "E363", {"start": v(51.47, 95.12) * mm, "end": v(51.53, 95.05) * mm});
            skLineSegment(sketch, "E364", {"start": v(51.53, 95.05) * mm, "end": v(51.58, 94.91) * mm});
            skLineSegment(sketch, "E365", {"start": v(51.58, 94.91) * mm, "end": v(51.61, 94.7) * mm});
            skLineSegment(sketch, "E366", {"start": v(51.61, 94.7) * mm, "end": v(51.62, 94.5) * mm});
            skLineSegment(sketch, "E367", {"start": v(51.62, 94.5) * mm, "end": v(51.63, 94.24) * mm});
            skLineSegment(sketch, "E368", {"start": v(50.6, 94.24) * mm, "end": v(50.6, 94.46) * mm});
            skLineSegment(sketch, "E369", {"start": v(50.6, 94.46) * mm, "end": v(50.6, 94.65) * mm});
            skLineSegment(sketch, "E370", {"start": v(50.6, 94.65) * mm, "end": v(50.62, 94.8) * mm});
            skLineSegment(sketch, "E371", {"start": v(50.62, 94.8) * mm, "end": v(50.65, 94.94) * mm});
            skLineSegment(sketch, "E372", {"start": v(50.65, 94.94) * mm, "end": v(50.69, 95.05) * mm});
            skLineSegment(sketch, "E373", {"start": v(50.69, 95.05) * mm, "end": v(50.75, 95.12) * mm});
            skLineSegment(sketch, "E374", {"start": v(50.75, 95.12) * mm, "end": v(50.84, 95.17) * mm});
            skLineSegment(sketch, "E375", {"start": v(50.84, 95.17) * mm, "end": v(50.96, 95.19) * mm});
            skLineSegment(sketch, "E376", {"start": v(50.96, 95.19) * mm, "end": v(51.11, 95.2) * mm});
            skLineSegment(sketch, "E377", {"start": v(51.11, 93.28) * mm, "end": v(50.96, 93.28) * mm});
            skLineSegment(sketch, "E378", {"start": v(50.96, 93.28) * mm, "end": v(50.84, 93.3) * mm});
            skLineSegment(sketch, "E379", {"start": v(50.84, 93.3) * mm, "end": v(50.75, 93.35) * mm});
            skLineSegment(sketch, "E380", {"start": v(50.75, 93.35) * mm, "end": v(50.69, 93.42) * mm});
            skLineSegment(sketch, "E381", {"start": v(50.69, 93.42) * mm, "end": v(50.64, 93.56) * mm});
            skLineSegment(sketch, "E382", {"start": v(50.64, 93.56) * mm, "end": v(50.61, 93.76) * mm});
            skLineSegment(sketch, "E383", {"start": v(50.61, 93.76) * mm, "end": v(50.6, 93.97) * mm});
            skLineSegment(sketch, "E384", {"start": v(50.6, 93.97) * mm, "end": v(50.6, 94.24) * mm});
            skLineSegment(sketch, "E385", {"start": v(51.63, 94.24) * mm, "end": v(51.62, 94) * mm});
            skLineSegment(sketch, "E386", {"start": v(51.62, 94) * mm, "end": v(51.62, 93.82) * mm});
            skLineSegment(sketch, "E387", {"start": v(51.62, 93.82) * mm, "end": v(51.6, 93.67) * mm});
            skLineSegment(sketch, "E388", {"start": v(51.6, 93.67) * mm, "end": v(51.58, 93.53) * mm});
            skLineSegment(sketch, "E389", {"start": v(51.58, 93.53) * mm, "end": v(51.53, 93.42) * mm});
            skLineSegment(sketch, "E390", {"start": v(51.53, 93.42) * mm, "end": v(51.47, 93.35) * mm});
            skLineSegment(sketch, "E391", {"start": v(51.47, 93.35) * mm, "end": v(51.38, 93.3) * mm});
            skLineSegment(sketch, "E392", {"start": v(51.38, 93.3) * mm, "end": v(51.26, 93.28) * mm});
            skLineSegment(sketch, "E393", {"start": v(51.26, 93.28) * mm, "end": v(51.11, 93.28) * mm});
            skLineSegment(sketch, "E394", {"start": v(50.3, 94.24) * mm, "end": v(50.3, 93.86) * mm});
            skLineSegment(sketch, "E395", {"start": v(50.3, 93.86) * mm, "end": v(50.33, 93.57) * mm});
            skLineSegment(sketch, "E396", {"start": v(50.33, 93.57) * mm, "end": v(50.37, 93.4) * mm});
            skLineSegment(sketch, "E397", {"start": v(50.37, 93.4) * mm, "end": v(50.43, 93.25) * mm});
            skLineSegment(sketch, "E398", {"start": v(50.43, 93.25) * mm, "end": v(50.53, 93.14) * mm});
            skLineSegment(sketch, "E399", {"start": v(50.53, 93.14) * mm, "end": v(50.68, 93.06) * mm});
            skLineSegment(sketch, "E400", {"start": v(50.68, 93.06) * mm, "end": v(50.87, 93.02) * mm});
            skLineSegment(sketch, "E401", {"start": v(50.87, 93.02) * mm, "end": v(51.11, 93) * mm});
            skLineSegment(sketch, "E402", {"start": v(51.11, 95.46) * mm, "end": v(50.87, 95.45) * mm});
            skLineSegment(sketch, "E403", {"start": v(50.87, 95.45) * mm, "end": v(50.67, 95.4) * mm});
            skLineSegment(sketch, "E404", {"start": v(50.67, 95.4) * mm, "end": v(50.53, 95.32) * mm});
            skLineSegment(sketch, "E405", {"start": v(50.53, 95.32) * mm, "end": v(50.43, 95.2) * mm});
            skLineSegment(sketch, "E406", {"start": v(50.43, 95.2) * mm, "end": v(50.36, 95.04) * mm});
            skLineSegment(sketch, "E407", {"start": v(50.36, 95.04) * mm, "end": v(50.32, 94.83) * mm});
            skLineSegment(sketch, "E408", {"start": v(50.32, 94.83) * mm, "end": v(50.3, 94.56) * mm});
            skLineSegment(sketch, "E409", {"start": v(50.3, 94.56) * mm, "end": v(50.3, 94.24) * mm});
            skLineSegment(sketch, "E410", {"start": v(51.93, 94.24) * mm, "end": v(51.93, 94.56) * mm});
            skLineSegment(sketch, "E411", {"start": v(51.93, 94.56) * mm, "end": v(51.9, 94.83) * mm});
            skLineSegment(sketch, "E412", {"start": v(51.9, 94.83) * mm, "end": v(51.86, 95.04) * mm});
            skLineSegment(sketch, "E413", {"start": v(51.86, 95.04) * mm, "end": v(51.8, 95.2) * mm});
            skLineSegment(sketch, "E414", {"start": v(51.8, 95.2) * mm, "end": v(51.7, 95.32) * mm});
            skLineSegment(sketch, "E415", {"start": v(51.7, 95.32) * mm, "end": v(51.55, 95.4) * mm});
            skLineSegment(sketch, "E416", {"start": v(51.55, 95.4) * mm, "end": v(51.36, 95.45) * mm});
            skLineSegment(sketch, "E417", {"start": v(51.36, 95.45) * mm, "end": v(51.11, 95.46) * mm});
            skLineSegment(sketch, "E418", {"start": v(48.99, 93.93) * mm, "end": v(48.98, 94.2) * mm});
            skLineSegment(sketch, "E419", {"start": v(48.98, 94.2) * mm, "end": v(48.96, 94.43) * mm});
            skLineSegment(sketch, "E420", {"start": v(48.96, 94.43) * mm, "end": v(48.9, 94.6) * mm});
            skLineSegment(sketch, "E421", {"start": v(48.9, 94.6) * mm, "end": v(48.83, 94.7) * mm});
            skLineSegment(sketch, "E422", {"start": v(48.83, 94.7) * mm, "end": v(48.73, 94.77) * mm});
            skLineSegment(sketch, "E423", {"start": v(48.73, 94.77) * mm, "end": v(48.6, 94.82) * mm});
            skLineSegment(sketch, "E424", {"start": v(48.68, 94) * mm, "end": v(48.68, 93.8) * mm});
            skLineSegment(sketch, "E425", {"start": v(48.68, 93.8) * mm, "end": v(48.66, 93.64) * mm});
            skLineSegment(sketch, "E426", {"start": v(48.66, 93.64) * mm, "end": v(48.62, 93.55) * mm});
            skLineSegment(sketch, "E427", {"start": v(48.62, 93.55) * mm, "end": v(48.57, 93.47) * mm});
            skLineSegment(sketch, "E428", {"start": v(48.57, 93.47) * mm, "end": v(48.47, 93.41) * mm});
            skLineSegment(sketch, "E429", {"start": v(48.47, 93.41) * mm, "end": v(48.33, 93.38) * mm});
            skLineSegment(sketch, "E430", {"start": v(48.33, 93.38) * mm, "end": v(48.15, 93.37) * mm});
            skLineSegment(sketch, "E431", {"start": v(48.15, 94.63) * mm, "end": v(48.33, 94.62) * mm});
            skLineSegment(sketch, "E432", {"start": v(48.33, 94.62) * mm, "end": v(48.46, 94.6) * mm});
            skLineSegment(sketch, "E433", {"start": v(48.46, 94.6) * mm, "end": v(48.55, 94.54) * mm});
            skLineSegment(sketch, "E434", {"start": v(48.55, 94.54) * mm, "end": v(48.62, 94.46) * mm});
            skLineSegment(sketch, "E435", {"start": v(48.62, 94.46) * mm, "end": v(48.66, 94.34) * mm});
            skLineSegment(sketch, "E436", {"start": v(48.66, 94.34) * mm, "end": v(48.68, 94.2) * mm});
            skLineSegment(sketch, "E437", {"start": v(48.68, 94.2) * mm, "end": v(48.68, 94) * mm});
            skLineSegment(sketch, "E438", {"start": v(48.62, 95.53) * mm, "end": v(48.6, 95.3) * mm});
            skLineSegment(sketch, "E439", {"start": v(48.6, 95.3) * mm, "end": v(48.55, 95.11) * mm});
            skLineSegment(sketch, "E440", {"start": v(48.55, 95.11) * mm, "end": v(48.5, 95.05) * mm});
            skLineSegment(sketch, "E441", {"start": v(48.5, 95.05) * mm, "end": v(48.42, 95) * mm});
            skLineSegment(sketch, "E442", {"start": v(48.42, 95) * mm, "end": v(48.33, 94.97) * mm});
            skLineSegment(sketch, "E443", {"start": v(48.33, 94.97) * mm, "end": v(48.2, 94.96) * mm});
            skLineSegment(sketch, "E444", {"start": v(48.23, 96.1) * mm, "end": v(48.35, 96.09) * mm});
            skLineSegment(sketch, "E445", {"start": v(48.35, 96.09) * mm, "end": v(48.45, 96.06) * mm});
            skLineSegment(sketch, "E446", {"start": v(48.45, 96.06) * mm, "end": v(48.52, 96) * mm});
            skLineSegment(sketch, "E447", {"start": v(48.52, 96) * mm, "end": v(48.57, 95.94) * mm});
            skLineSegment(sketch, "E448", {"start": v(48.57, 95.94) * mm, "end": v(48.6, 95.83) * mm});
            skLineSegment(sketch, "E449", {"start": v(48.6, 95.83) * mm, "end": v(48.62, 95.69) * mm});
            skLineSegment(sketch, "E450", {"start": v(48.62, 95.69) * mm, "end": v(48.62, 95.53) * mm});
            skLineSegment(sketch, "E451", {"start": v(48.93, 95.62) * mm, "end": v(48.91, 95.9) * mm});
            skLineSegment(sketch, "E452", {"start": v(48.91, 95.9) * mm, "end": v(48.86, 96.11) * mm});
            skLineSegment(sketch, "E453", {"start": v(48.86, 96.11) * mm, "end": v(48.75, 96.27) * mm});
            skLineSegment(sketch, "E454", {"start": v(48.75, 96.27) * mm, "end": v(48.62, 96.36) * mm});
            skLineSegment(sketch, "E455", {"start": v(48.62, 96.36) * mm, "end": v(48.45, 96.4) * mm});
            skLineSegment(sketch, "E456", {"start": v(48.45, 96.4) * mm, "end": v(48.22, 96.42) * mm});
            skLineSegment(sketch, "E457", {"start": v(48.22, 93.04) * mm, "end": v(48.45, 93.06) * mm});
            skLineSegment(sketch, "E458", {"start": v(48.45, 93.06) * mm, "end": v(48.63, 93.11) * mm});
            skLineSegment(sketch, "E459", {"start": v(48.63, 93.11) * mm, "end": v(48.77, 93.2) * mm});
            skLineSegment(sketch, "E460", {"start": v(48.77, 93.2) * mm, "end": v(48.87, 93.32) * mm});
            skLineSegment(sketch, "E461", {"start": v(48.87, 93.32) * mm, "end": v(48.94, 93.48) * mm});
            skLineSegment(sketch, "E462", {"start": v(48.94, 93.48) * mm, "end": v(48.98, 93.69) * mm});
            skLineSegment(sketch, "E463", {"start": v(48.98, 93.69) * mm, "end": v(48.99, 93.93) * mm});
            skLineSegment(sketch, "E464", {"start": v(39.12, 91.53) * mm, "end": v(39.27, 91.03) * mm});
            skLineSegment(sketch, "E465", {"start": v(39.35, 91.03) * mm, "end": v(39.12, 91.53) * mm});
            skLineSegment(sketch, "E466", {"start": v(39.07, 93.1) * mm, "end": v(39.07, 93.1) * mm});
            skLineSegment(sketch, "E467", {"start": v(43.7, 87.64) * mm, "end": v(43.76, 87.64) * mm});
            skLineSegment(sketch, "E468", {"start": v(44.13, 93.84) * mm, "end": v(44.15, 93.86) * mm});
            skLineSegment(sketch, "E469", {"start": v(68.02, 93.04) * mm, "end": v(68.02, 94.73) * mm});
            skLineSegment(sketch, "E470", {"start": v(67.74, 93.04) * mm, "end": v(68.02, 93.04) * mm});
            skLineSegment(sketch, "E471", {"start": v(67.74, 94.65) * mm, "end": v(67.74, 93.04) * mm});
            skLineSegment(sketch, "E472", {"start": v(66.75, 93.04) * mm, "end": v(66.75, 94.55) * mm});
            skLineSegment(sketch, "E473", {"start": v(66.47, 93.04) * mm, "end": v(66.75, 93.04) * mm});
            skLineSegment(sketch, "E474", {"start": v(66.47, 96.42) * mm, "end": v(66.47, 93.04) * mm});
            skLineSegment(sketch, "E475", {"start": v(66.75, 96.42) * mm, "end": v(66.47, 96.42) * mm});
            skLineSegment(sketch, "E476", {"start": v(66.75, 95.12) * mm, "end": v(66.75, 96.42) * mm});
            skLineSegment(sketch, "E477", {"start": v(66.75, 95.12) * mm, "end": v(66.75, 95.12) * mm});
            skLineSegment(sketch, "E478", {"start": v(66.08, 93.9) * mm, "end": v(65.8, 93.9) * mm});
            skLineSegment(sketch, "E479", {"start": v(66.08, 93.75) * mm, "end": v(66.08, 93.9) * mm});
            skLineSegment(sketch, "E480", {"start": v(65.76, 94.63) * mm, "end": v(66.04, 94.63) * mm});
            skLineSegment(sketch, "E481", {"start": v(64.07, 93.75) * mm, "end": v(63.8, 93.75) * mm});
            skLineSegment(sketch, "E482", {"start": v(63.8, 94.46) * mm, "end": v(62.78, 94.46) * mm});
            skLineSegment(sketch, "E483", {"start": v(64.07, 93.67) * mm, "end": v(64.07, 93.75) * mm});
            skLineSegment(sketch, "E484", {"start": v(64.07, 94.17) * mm, "end": v(64.07, 94.52) * mm});
            skLineSegment(sketch, "E485", {"start": v(62.78, 94.17) * mm, "end": v(64.07, 94.17) * mm});
            skLineSegment(sketch, "E486", {"start": v(62.78, 93.95) * mm, "end": v(62.78, 94.17) * mm});
            skLineSegment(sketch, "E487", {"start": v(60.62, 96.42) * mm, "end": v(60.62, 96.1) * mm});
            skLineSegment(sketch, "E488", {"start": v(62.65, 96.42) * mm, "end": v(60.62, 96.42) * mm});
            skLineSegment(sketch, "E489", {"start": v(62.65, 96.1) * mm, "end": v(62.65, 96.42) * mm});
            skLineSegment(sketch, "E490", {"start": v(61.8, 96.1) * mm, "end": v(62.65, 96.1) * mm});
            skLineSegment(sketch, "E491", {"start": v(61.8, 93.04) * mm, "end": v(61.8, 96.1) * mm});
            skLineSegment(sketch, "E492", {"start": v(61.49, 93.04) * mm, "end": v(61.8, 93.04) * mm});
            skLineSegment(sketch, "E493", {"start": v(61.49, 96.1) * mm, "end": v(61.49, 93.04) * mm});
            skLineSegment(sketch, "E494", {"start": v(60.62, 96.1) * mm, "end": v(61.49, 96.1) * mm});
            skLineSegment(sketch, "E495", {"start": v(60.29, 96.03) * mm, "end": v(60.29, 96.42) * mm});
            skLineSegment(sketch, "E496", {"start": v(60, 96.03) * mm, "end": v(60.29, 96.03) * mm});
            skLineSegment(sketch, "E497", {"start": v(60, 96.42) * mm, "end": v(60, 96.03) * mm});
            skLineSegment(sketch, "E498", {"start": v(60.29, 96.42) * mm, "end": v(60, 96.42) * mm});
            skLineSegment(sketch, "E499", {"start": v(60.29, 93.04) * mm, "end": v(60.29, 95.43) * mm});
            skLineSegment(sketch, "E500", {"start": v(60, 93.04) * mm, "end": v(60.29, 93.04) * mm});
            skLineSegment(sketch, "E501", {"start": v(60, 95.43) * mm, "end": v(60, 93.04) * mm});
            skLineSegment(sketch, "E502", {"start": v(60.29, 95.43) * mm, "end": v(60, 95.43) * mm});
            skLineSegment(sketch, "E503", {"start": v(59.17, 95.13) * mm, "end": v(59.16, 95.13) * mm});
            skLineSegment(sketch, "E504", {"start": v(59.17, 96.42) * mm, "end": v(59.17, 95.13) * mm});
            skLineSegment(sketch, "E505", {"start": v(59.45, 96.42) * mm, "end": v(59.17, 96.42) * mm});
            skLineSegment(sketch, "E506", {"start": v(59.45, 93.04) * mm, "end": v(59.45, 96.42) * mm});
            skLineSegment(sketch, "E507", {"start": v(59.17, 93.04) * mm, "end": v(59.45, 93.04) * mm});
            skLineSegment(sketch, "E508", {"start": v(59.17, 93.34) * mm, "end": v(59.17, 93.04) * mm});
            skLineSegment(sketch, "E509", {"start": v(59.16, 93.34) * mm, "end": v(59.17, 93.34) * mm});
            skLineSegment(sketch, "E510", {"start": v(57.38, 93.75) * mm, "end": v(57.1, 93.75) * mm});
            skLineSegment(sketch, "E511", {"start": v(57.1, 94.46) * mm, "end": v(56.09, 94.46) * mm});
            skLineSegment(sketch, "E512", {"start": v(57.38, 93.67) * mm, "end": v(57.38, 93.75) * mm});
            skLineSegment(sketch, "E513", {"start": v(57.38, 94.17) * mm, "end": v(57.38, 94.52) * mm});
            skLineSegment(sketch, "E514", {"start": v(56.09, 94.17) * mm, "end": v(57.38, 94.17) * mm});
            skLineSegment(sketch, "E515", {"start": v(56.09, 93.95) * mm, "end": v(56.09, 94.17) * mm});
            skLineSegment(sketch, "E516", {"start": v(53.85, 93.44) * mm, "end": v(52.9, 96.42) * mm});
            skLineSegment(sketch, "E517", {"start": v(53.86, 93.44) * mm, "end": v(53.85, 93.44) * mm});
            skLineSegment(sketch, "E518", {"start": v(54.81, 96.42) * mm, "end": v(53.86, 93.44) * mm});
            skLineSegment(sketch, "E519", {"start": v(55.32, 96.42) * mm, "end": v(54.81, 96.42) * mm});
            skLineSegment(sketch, "E520", {"start": v(55.32, 93.04) * mm, "end": v(55.32, 96.42) * mm});
            skLineSegment(sketch, "E521", {"start": v(55.02, 93.04) * mm, "end": v(55.32, 93.04) * mm});
            skLineSegment(sketch, "E522", {"start": v(55.02, 96.07) * mm, "end": v(55.02, 93.04) * mm});
            skLineSegment(sketch, "E523", {"start": v(55.01, 96.07) * mm, "end": v(55.02, 96.07) * mm});
            skLineSegment(sketch, "E524", {"start": v(54.02, 93.04) * mm, "end": v(55.01, 96.07) * mm});
            skLineSegment(sketch, "E525", {"start": v(53.7, 93.04) * mm, "end": v(54.02, 93.04) * mm});
            skLineSegment(sketch, "E526", {"start": v(52.7, 96.07) * mm, "end": v(53.7, 93.04) * mm});
            skLineSegment(sketch, "E527", {"start": v(52.7, 96.07) * mm, "end": v(52.7, 96.07) * mm});
            skLineSegment(sketch, "E528", {"start": v(52.7, 93.04) * mm, "end": v(52.7, 96.07) * mm});
            skLineSegment(sketch, "E529", {"start": v(52.39, 93.04) * mm, "end": v(52.7, 93.04) * mm});
            skLineSegment(sketch, "E530", {"start": v(52.39, 96.42) * mm, "end": v(52.39, 93.04) * mm});
            skLineSegment(sketch, "E531", {"start": v(52.9, 96.42) * mm, "end": v(52.39, 96.42) * mm});
            skLineSegment(sketch, "E532", {"start": v(49.8, 96.03) * mm, "end": v(49.8, 96.42) * mm});
            skLineSegment(sketch, "E533", {"start": v(49.52, 96.03) * mm, "end": v(49.8, 96.03) * mm});
            skLineSegment(sketch, "E534", {"start": v(49.8, 96.42) * mm, "end": v(49.52, 96.42) * mm});
            skLineSegment(sketch, "E535", {"start": v(49.52, 96.42) * mm, "end": v(49.52, 96.03) * mm});
            skLineSegment(sketch, "E536", {"start": v(49.8, 93.04) * mm, "end": v(49.8, 95.43) * mm});
            skLineSegment(sketch, "E537", {"start": v(49.52, 93.04) * mm, "end": v(49.8, 93.04) * mm});
            skLineSegment(sketch, "E538", {"start": v(49.8, 95.43) * mm, "end": v(49.52, 95.43) * mm});
            skLineSegment(sketch, "E539", {"start": v(49.52, 95.43) * mm, "end": v(49.52, 93.04) * mm});
            skLineSegment(sketch, "E540", {"start": v(48.6, 94.82) * mm, "end": v(48.6, 94.83) * mm});
            skLineSegment(sketch, "E541", {"start": v(46.98, 93.04) * mm, "end": v(48.22, 93.04) * mm});
            skLineSegment(sketch, "E542", {"start": v(46.98, 96.42) * mm, "end": v(46.98, 93.04) * mm});
            skLineSegment(sketch, "E543", {"start": v(48.22, 96.42) * mm, "end": v(46.98, 96.42) * mm});
            skLineSegment(sketch, "E544", {"start": v(47.28, 93.37) * mm, "end": v(47.28, 94.63) * mm});
            skLineSegment(sketch, "E545", {"start": v(47.28, 96.1) * mm, "end": v(48.23, 96.1) * mm});
            skLineSegment(sketch, "E546", {"start": v(47.28, 94.96) * mm, "end": v(47.28, 96.1) * mm});
            skLineSegment(sketch, "E547", {"start": v(48.2, 94.96) * mm, "end": v(47.28, 94.96) * mm});
            skLineSegment(sketch, "E548", {"start": v(48.15, 93.37) * mm, "end": v(47.28, 93.37) * mm});
            skLineSegment(sketch, "E549", {"start": v(47.28, 94.63) * mm, "end": v(48.15, 94.63) * mm});
            skArc(sketch, "E550", {"start": v(41.42, 96.03) * mm, "mid": v(40.04, 97.04) * mm, "end": v(38.43, 97.6) * mm});
            skArc(sketch, "E551", {"start": v(36.62, 94.25) * mm, "mid": v(37.63, 92.22) * mm, "end": v(39.38, 90.77) * mm});
            skArc(sketch, "E552", {"start": v(44.18, 91.79) * mm, "mid": v(43.05, 93.23) * mm, "end": v(41.4, 94.03) * mm});
            skArc(sketch, "E553", {"start": v(41.4, 94.03) * mm, "mid": v(41.76, 93.51) * mm, "end": v(42.34, 93.27) * mm});
            skArc(sketch, "E554", {"start": v(41.04, 94.1) * mm, "mid": v(41.57, 93.5) * mm, "end": v(42.34, 93.27) * mm});
            skArc(sketch, "E555", {"start": v(40.9, 94.83) * mm, "mid": v(39.65, 94.32) * mm, "end": v(39.07, 93.1) * mm});
            skArc(sketch, "E556", {"start": v(41.42, 96.03) * mm, "mid": v(41.13, 95.45) * mm, "end": v(40.97, 94.83) * mm});
            skArc(sketch, "E557", {"start": v(42.4, 94.68) * mm, "mid": v(42.15, 95.18) * mm, "end": v(41.83, 95.65) * mm});
            skArc(sketch, "E558", {"start": v(42.4, 94.68) * mm, "mid": v(42.13, 95.16) * mm, "end": v(41.8, 95.61) * mm});
            skArc(sketch, "E559", {"start": v(41.8, 95.61) * mm, "mid": v(41.56, 95.21) * mm, "end": v(41.41, 94.77) * mm});
            skArc(sketch, "E560", {"start": v(39.84, 90.04) * mm, "mid": v(41.32, 88.54) * mm, "end": v(43.25, 87.68) * mm});
            skArc(sketch, "E561", {"start": v(35.63, 93.55) * mm, "mid": v(37.33, 91.3) * mm, "end": v(39.84, 90.04) * mm});
            skArc(sketch, "E562", {"start": v(37.3, 98.25) * mm, "mid": v(36.13, 97.9) * mm, "end": v(35.3, 97.01) * mm});
            skArc(sketch, "E563", {"start": v(41.46, 96.1) * mm, "mid": v(39.8, 97.45) * mm, "end": v(37.8, 98.2) * mm});
            skArc(sketch, "E564", {"start": v(45.66, 96.37) * mm, "mid": v(45.41, 97.47) * mm, "end": v(44.38, 97.93) * mm});
            skArc(sketch, "E565", {"start": v(44.13, 93.84) * mm, "mid": v(45.15, 94.95) * mm, "end": v(45.66, 96.37) * mm});
            skArc(sketch, "E566", {"start": v(44.15, 93.86) * mm, "mid": v(44.93, 94.73) * mm, "end": v(45.3, 95.84) * mm});
            skArc(sketch, "E567", {"start": v(43.35, 96.64) * mm, "mid": v(42.52, 96.25) * mm, "end": v(41.83, 95.65) * mm});
            skArc(sketch, "E568", {"start": v(43.57, 97.79) * mm, "mid": v(42.38, 97.12) * mm, "end": v(41.46, 96.1) * mm});
            skArc(sketch, "E569", {"start": v(44.38, 97.93) * mm, "mid": v(43.97, 97.9) * mm, "end": v(43.57, 97.79) * mm});
            skArc(sketch, "E570", {"start": v(67.37, 95.46) * mm, "mid": v(67, 95.39) * mm, "end": v(66.75, 95.12) * mm});
            skArc(sketch, "E571", {"start": v(59.16, 95.13) * mm, "mid": v(58.9, 95.39) * mm, "end": v(58.54, 95.46) * mm});
            skArc(sketch, "E572", {"start": v(58.59, 93) * mm, "mid": v(58.93, 93.08) * mm, "end": v(59.16, 93.34) * mm});
            skArc(sketch, "E573", {"start": v(48.6, 94.83) * mm, "mid": v(48.9, 95.17) * mm, "end": v(48.93, 95.62) * mm});
            skLineSegment(sketch, "E574.bottom", {"start": v(33.92, 101.45) * mm, "end": v(70.36, 101.45) * mm});
            skLineSegment(sketch, "E574.top", {"start": v(33.92, 86.45) * mm, "end": v(70.36, 86.45) * mm});
            skLineSegment(sketch, "E574.left", {"start": v(33.92, 101.45) * mm, "end": v(33.92, 86.45) * mm});
            skLineSegment(sketch, "E574.right", {"start": v(70.36, 101.45) * mm, "end": v(70.36, 86.45) * mm});
            skSolve(sketch);
        }
        {
            var Q0;
            Q0=makeQuery(id+"F0.imprint","IMPRINT",FACE,{"disambiguationData":[TD([[makeQuery(id+"F0.imprint","IMPRINT",EDGE,{"derivedFrom":sQuery(id+"F0.wireOp",EDGE,"E67")}),-1.0]])]});
            var Q1;
            Q1=makeQuery(id+"F0.imprint","IMPRINT",FACE,{"disambiguationData":[TD([[makeQuery(id+"F0.imprint","IMPRINT",EDGE,{"derivedFrom":sQuery(id+"F0.wireOp",EDGE,"E0")}),1.0]])]});
            var Q2;
            Q2=makeQuery(id+"F0.imprint","IMPRINT",FACE,{"disambiguationData":[TD([[makeQuery(id+"F0.imprint","IMPRINT",EDGE,{"derivedFrom":sQuery(id+"F0.wireOp",EDGE,"E424")}),-1.0]])]});
            var Q3;
            Q3=makeQuery(id+"F0.imprint","IMPRINT",FACE,{"disambiguationData":[TD([[makeQuery(id+"F0.imprint","IMPRINT",EDGE,{"derivedFrom":sQuery(id+"F0.wireOp",EDGE,"E438")}),-1.0]])]});
            var Q4;
            Q4=makeQuery(id+"F0.imprint","IMPRINT",FACE,{"disambiguationData":[TD([[makeQuery(id+"F0.imprint","IMPRINT",EDGE,{"derivedFrom":sQuery(id+"F0.wireOp",EDGE,"E188")}),-1.0]])]});
            var Q5;
            Q5=makeQuery(id+"F0.imprint","IMPRINT",FACE,{"disambiguationData":[TD([[makeQuery(id+"F0.imprint","IMPRINT",EDGE,{"derivedFrom":sQuery(id+"F0.wireOp",EDGE,"E111")}),1.0]])]});
            var Q6;
            Q6=makeQuery(id+"F0.imprint","IMPRINT",FACE,{"disambiguationData":[TD([[makeQuery(id+"F0.imprint","IMPRINT",EDGE,{"derivedFrom":sQuery(id+"F0.wireOp",EDGE,"E0")}),-1.0]])]});
            var Q7;
            Q7=makeQuery(id+"F0.imprint","IMPRINT",FACE,{"disambiguationData":[TD([[makeQuery(id+"F0.imprint","IMPRINT",EDGE,{"derivedFrom":sQuery(id+"F0.wireOp",EDGE,"E536")}),1.0]])]});
            var Q8;
            Q8=makeQuery(id+"F0.imprint","IMPRINT",FACE,{"disambiguationData":[TD([[makeQuery(id+"F0.imprint","IMPRINT",EDGE,{"derivedFrom":sQuery(id+"F0.wireOp",EDGE,"E418")}),1.0]])]});
            var Q9;
            Q9=makeQuery(id+"F0.imprint","IMPRINT",FACE,{"disambiguationData":[TD([[makeQuery(id+"F0.imprint","IMPRINT",EDGE,{"derivedFrom":sQuery(id+"F0.wireOp",EDGE,"E293")}),1.0]])]});
            var Q10;
            Q10=makeQuery(id+"F0.imprint","IMPRINT",FACE,{"disambiguationData":[TD([[makeQuery(id+"F0.imprint","IMPRINT",EDGE,{"derivedFrom":sQuery(id+"F0.wireOp",EDGE,"E247")}),1.0]])]});
            var Q11;
            Q11=makeQuery(id+"F0.imprint","IMPRINT",FACE,{"disambiguationData":[TD([[makeQuery(id+"F0.imprint","IMPRINT",EDGE,{"derivedFrom":sQuery(id+"F0.wireOp",EDGE,"E188")}),1.0]])]});
            var Q12;
            Q12=makeQuery(id+"F0.imprint","IMPRINT",FACE,{"disambiguationData":[TD([[makeQuery(id+"F0.imprint","IMPRINT",EDGE,{"derivedFrom":sQuery(id+"F0.wireOp",EDGE,"E255")}),-1.0]])]});
            var Q13;
            Q13=makeQuery(id+"F0.imprint","IMPRINT",FACE,{"disambiguationData":[TD([[makeQuery(id+"F0.imprint","IMPRINT",EDGE,{"derivedFrom":sQuery(id+"F0.wireOp",EDGE,"E293")}),-1.0]])]});
            var Q14;
            Q14=makeQuery(id+"F0.imprint","IMPRINT",FACE,{"disambiguationData":[TD([[makeQuery(id+"F0.imprint","IMPRINT",EDGE,{"derivedFrom":sQuery(id+"F0.wireOp",EDGE,"E360")}),-1.0]])]});
            var Q15;
            Q15=makeQuery(id+"F0.imprint","IMPRINT",FACE,{"disambiguationData":[TD([[makeQuery(id+"F0.imprint","IMPRINT",EDGE,{"derivedFrom":sQuery(id+"F0.wireOp",EDGE,"E487")}),1.0]])]});
            var Q16;
            Q16=makeQuery(id+"F0.imprint","IMPRINT",FACE,{"disambiguationData":[TD([[makeQuery(id+"F0.imprint","IMPRINT",EDGE,{"derivedFrom":sQuery(id+"F0.wireOp",EDGE,"E499")}),1.0]])]});
            var Q17;
            Q17=makeQuery(id+"F0.imprint","IMPRINT",FACE,{"disambiguationData":[TD([[makeQuery(id+"F0.imprint","IMPRINT",EDGE,{"derivedFrom":sQuery(id+"F0.wireOp",EDGE,"E516")}),1.0]])]});
            var Q18;
            Q18=makeQuery(id+"F0.imprint","IMPRINT",FACE,{"disambiguationData":[TD([[makeQuery(id+"F0.imprint","IMPRINT",EDGE,{"derivedFrom":sQuery(id+"F0.wireOp",EDGE,"E129")}),1.0]])]});
            var Q19;
            Q19=makeQuery(id+"F0.imprint","IMPRINT",FACE,{"disambiguationData":[TD([[makeQuery(id+"F0.imprint","IMPRINT",EDGE,{"derivedFrom":sQuery(id+"F0.wireOp",EDGE,"E532")}),1.0]])]});
            var Q20;
            Q20=makeQuery(id+"F0.imprint","IMPRINT",FACE,{"disambiguationData":[TD([[makeQuery(id+"F0.imprint","IMPRINT",EDGE,{"derivedFrom":sQuery(id+"F0.wireOp",EDGE,"E352")}),1.0]])]});
            var Q21;
            Q21=makeQuery(id+"F0.imprint","IMPRINT",FACE,{"disambiguationData":[TD([[makeQuery(id+"F0.imprint","IMPRINT",EDGE,{"derivedFrom":sQuery(id+"F0.wireOp",EDGE,"E495")}),1.0]])]});
            extrude(context, id + "F1", {"entities" : qUnion([Q0, Q1, Q2, Q3, Q4, Q5, Q6, Q7, Q8, Q9, Q10, Q11, Q12, Q13, Q14, Q15, Q16, Q17, Q18, Q19, Q20, Q21]), "depth" : 5 * mm, "offsetDistance" : 25 * mm});
        }
        {
            var Q0;
            Q0=makeQuery(id+"F0.imprint","IMPRINT",FACE,{"disambiguationData":[TD([[makeQuery(id+"F0.imprint","IMPRINT",EDGE,{"derivedFrom":sQuery(id+"F0.wireOp",EDGE,"E0")}),1.0]])]});
            var Q1;
            Q1=makeQuery(id+"F0.imprint","IMPRINT",FACE,{"disambiguationData":[TD([[makeQuery(id+"F0.imprint","IMPRINT",EDGE,{"derivedFrom":sQuery(id+"F0.wireOp",EDGE,"E418")}),1.0]])]});
            var Q2;
            Q2=makeQuery(id+"F0.imprint","IMPRINT",FACE,{"disambiguationData":[TD([[makeQuery(id+"F0.imprint","IMPRINT",EDGE,{"derivedFrom":sQuery(id+"F0.wireOp",EDGE,"E536")}),1.0]])]});
            var Q3;
            Q3=makeQuery(id+"F0.imprint","IMPRINT",FACE,{"disambiguationData":[TD([[makeQuery(id+"F0.imprint","IMPRINT",EDGE,{"derivedFrom":sQuery(id+"F0.wireOp",EDGE,"E532")}),1.0]])]});
            var Q4;
            Q4=makeQuery(id+"F0.imprint","IMPRINT",FACE,{"disambiguationData":[TD([[makeQuery(id+"F0.imprint","IMPRINT",EDGE,{"derivedFrom":sQuery(id+"F0.wireOp",EDGE,"E352")}),1.0]])]});
            var Q5;
            Q5=makeQuery(id+"F0.imprint","IMPRINT",FACE,{"disambiguationData":[TD([[makeQuery(id+"F0.imprint","IMPRINT",EDGE,{"derivedFrom":sQuery(id+"F0.wireOp",EDGE,"E516")}),1.0]])]});
            var Q6;
            Q6=makeQuery(id+"F0.imprint","IMPRINT",FACE,{"disambiguationData":[TD([[makeQuery(id+"F0.imprint","IMPRINT",EDGE,{"derivedFrom":sQuery(id+"F0.wireOp",EDGE,"E293")}),1.0]])]});
            var Q7;
            Q7=makeQuery(id+"F0.imprint","IMPRINT",FACE,{"disambiguationData":[TD([[makeQuery(id+"F0.imprint","IMPRINT",EDGE,{"derivedFrom":sQuery(id+"F0.wireOp",EDGE,"E499")}),1.0]])]});
            var Q8;
            Q8=makeQuery(id+"F0.imprint","IMPRINT",FACE,{"disambiguationData":[TD([[makeQuery(id+"F0.imprint","IMPRINT",EDGE,{"derivedFrom":sQuery(id+"F0.wireOp",EDGE,"E495")}),1.0]])]});
            var Q9;
            Q9=makeQuery(id+"F0.imprint","IMPRINT",FACE,{"disambiguationData":[TD([[makeQuery(id+"F0.imprint","IMPRINT",EDGE,{"derivedFrom":sQuery(id+"F0.wireOp",EDGE,"E487")}),1.0]])]});
            var Q10;
            Q10=makeQuery(id+"F0.imprint","IMPRINT",FACE,{"disambiguationData":[TD([[makeQuery(id+"F0.imprint","IMPRINT",EDGE,{"derivedFrom":sQuery(id+"F0.wireOp",EDGE,"E188")}),1.0]])]});
            var Q11;
            Q11=makeQuery(id+"F0.imprint","IMPRINT",FACE,{"disambiguationData":[TD([[makeQuery(id+"F0.imprint","IMPRINT",EDGE,{"derivedFrom":sQuery(id+"F0.wireOp",EDGE,"E129")}),1.0]])]});
            var Q12;
            Q12=makeQuery(id+"F0.imprint","IMPRINT",FACE,{"disambiguationData":[TD([[makeQuery(id+"F0.imprint","IMPRINT",EDGE,{"derivedFrom":sQuery(id+"F0.wireOp",EDGE,"E111")}),1.0]])]});
            var Q13;
            Q13=makeQuery(id+"F0.imprint","IMPRINT",FACE,{"disambiguationData":[TD([[makeQuery(id+"F0.imprint","IMPRINT",EDGE,{"derivedFrom":sQuery(id+"F0.wireOp",EDGE,"E247")}),1.0]])]});
            extrude(context, id + "F2", {"entities" : qUnion([Q0, Q1, Q2, Q3, Q4, Q5, Q6, Q7, Q8, Q9, Q10, Q11, Q12, Q13]), "operationType" : NewBodyOperationType.ADD, "oppositeDirection" : true, "depth" : 25 * mm, "offsetDistance" : 25 * mm});
        }
    });
